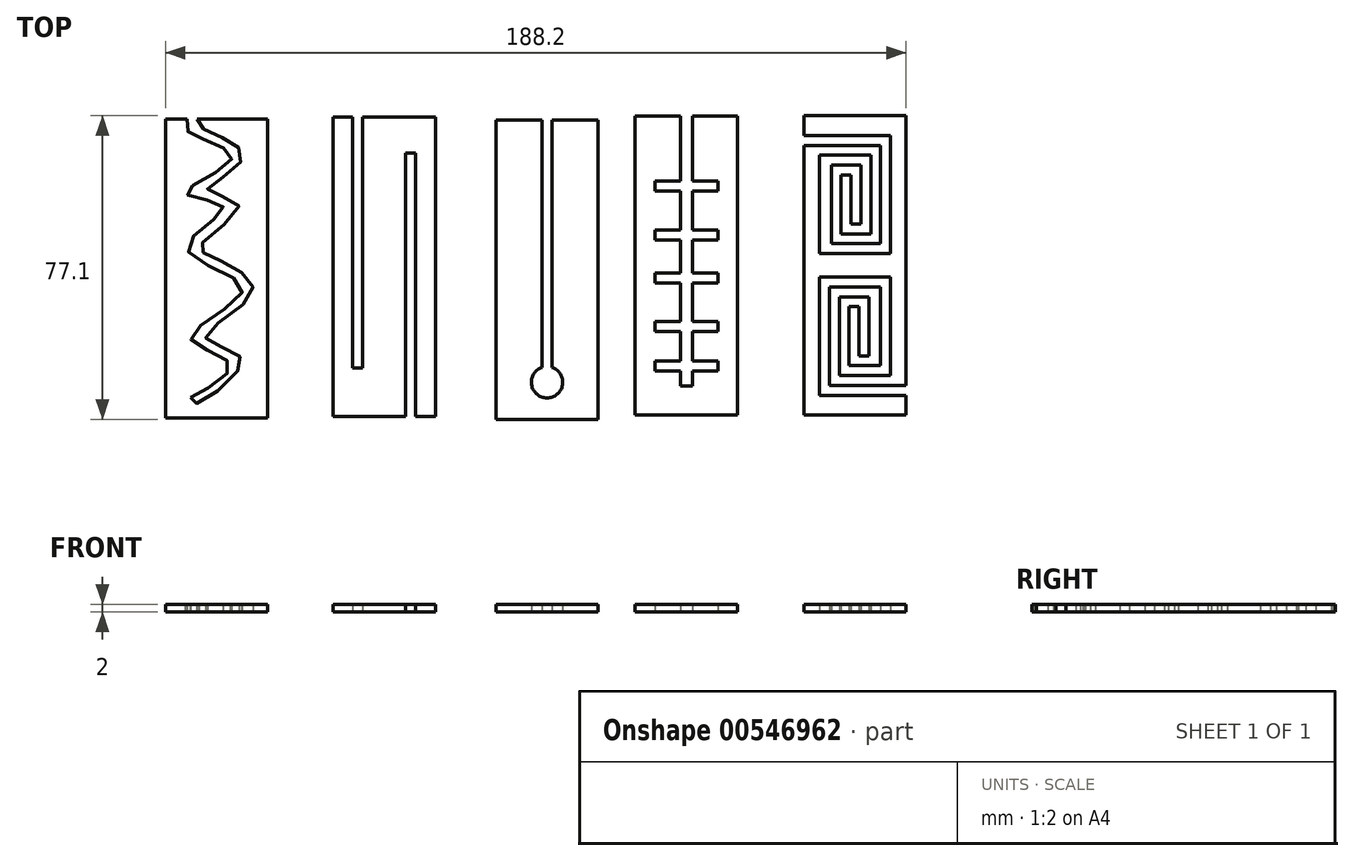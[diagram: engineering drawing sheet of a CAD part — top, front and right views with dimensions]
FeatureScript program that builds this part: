
annotation { "Feature Type Name" : "Feature", "Feature Type Description" : "" }
export const myFeature = defineFeature(function(context is Context, id is Id, definition is map)
    precondition{}
    {
        {
            var Q0;
            Q0=qCreatedBy(makeId("Top.planeOp"),FACE);
            var sketch = newSketch(context, id + "F0", { "sketchPlane" : qUnion([Q0])});
            skLineSegment(sketch, "E0.bottom", {"start": v(-60.07, 57.75) * mm, "end": v(-34.07, 57.75) * mm});
            skLineSegment(sketch, "E0.top", {"start": v(-60.07, -18.25) * mm, "end": v(-34.07, -18.25) * mm});
            skLineSegment(sketch, "E0.left", {"start": v(-60.07, 57.75) * mm, "end": v(-60.07, -18.25) * mm});
            skLineSegment(sketch, "E0.right", {"start": v(-34.07, 57.75) * mm, "end": v(-34.07, -18.25) * mm});
            skFitSpline(sketch, "E1", {"points": [v(-54.5, 57.75) * mm, v(-52.59, 53.49) * mm, v(-43.2, 47.62) * mm, v(-54.81, 38.91) * mm, v(-45.36, 35.29) * mm, v(-54.59, 24.98) * mm, v(-40.4, 14.57) * mm, v(-53.66, 2.1) * mm, v(-43.58, -4.75) * mm, v(-53.63, -13.02) * mm], "startDerivative": vector(-39.3, -111.57) * mm, "endDerivative": vector(-54.15, -27.59) * mm});
            skFitSpline(sketch, "E2", {"points": [v(-52, 57.75) * mm, v(-49.93, 55) * mm, v(-41.52, 50.54) * mm, v(-41.87, 45.6) * mm, v(-49.3, 39.6) * mm, v(-41.4, 35.83) * mm, v(-51.17, 25.7) * mm, v(-50.23, 23.7) * mm, v(-40.34, 18.4) * mm, v(-38.46, 12.52) * mm, v(-49.88, 2.4) * mm, v(-42, -1.84) * mm, v(-41.64, -6.2) * mm, v(-52.86, -14.54) * mm, v(-53.63, -13.02) * mm], "startDerivative": vector(-29.1, -66.37) * mm, "endDerivative": vector(-0.83, 52.83) * mm});
            skLineSegment(sketch, "E3.bottom", {"start": v(-17.5, 58.21) * mm, "end": v(8.5, 58.21) * mm});
            skLineSegment(sketch, "E3.top", {"start": v(-17.5, -17.79) * mm, "end": v(8.5, -17.79) * mm});
            skLineSegment(sketch, "E3.left", {"start": v(-17.5, 58.21) * mm, "end": v(-17.5, -17.79) * mm});
            skLineSegment(sketch, "E3.right", {"start": v(8.5, 58.21) * mm, "end": v(8.5, -17.79) * mm});
            skLineSegment(sketch, "E4.bottom", {"start": v(23.9, 57.45) * mm, "end": v(35.64, 57.45) * mm});
            skLineSegment(sketch, "E4.top", {"start": v(23.9, -18.55) * mm, "end": v(49.9, -18.55) * mm});
            skLineSegment(sketch, "E4.left", {"start": v(23.9, 57.45) * mm, "end": v(23.9, -18.55) * mm});
            skLineSegment(sketch, "E4.right", {"start": v(49.9, 57.45) * mm, "end": v(49.9, -18.55) * mm});
            skLineSegment(sketch, "E5.bottom", {"start": v(59.3, 58.49) * mm, "end": v(70.8, 58.49) * mm});
            skLineSegment(sketch, "E5.top", {"start": v(59.3, -17.51) * mm, "end": v(85.3, -17.51) * mm});
            skLineSegment(sketch, "E5.left", {"start": v(59.3, 58.49) * mm, "end": v(59.3, -17.51) * mm});
            skLineSegment(sketch, "E5.right", {"start": v(85.3, 58.49) * mm, "end": v(85.3, -17.51) * mm});
            skLineSegment(sketch, "E6.bottom", {"start": v(102.13, 58.55) * mm, "end": v(128.13, 58.55) * mm});
            skLineSegment(sketch, "E6.top", {"start": v(102.13, -17.45) * mm, "end": v(128.13, -17.45) * mm});
            skLineSegment(sketch, "E6.left", {"start": v(102.13, 58.55) * mm, "end": v(102.13, -17.45) * mm});
            skLineSegment(sketch, "E6.right", {"start": v(128.13, 58.55) * mm, "end": v(128.13, -17.45) * mm});
            skLineSegment(sketch, "E7", {"start": v(-12.5, 58.21) * mm, "end": v(-12.5, -5.58) * mm});
            skLineSegment(sketch, "E8", {"start": v(-12.5, -5.58) * mm, "end": v(-10, -5.58) * mm});
            skLineSegment(sketch, "E9", {"start": v(-10, -5.58) * mm, "end": v(-10, 58.21) * mm});
            skLineSegment(sketch, "E10", {"start": v(1, -17.79) * mm, "end": v(1, 49.05) * mm});
            skLineSegment(sketch, "E11", {"start": v(1, 49.05) * mm, "end": v(3.5, 49.05) * mm});
            skLineSegment(sketch, "E12", {"start": v(3.5, 49.05) * mm, "end": v(3.5, -17.79) * mm});
            skLineSegment(sketch, "E13", {"start": v(35.64, 57.45) * mm, "end": v(35.64, -5.35) * mm});
            skLineSegment(sketch, "E14", {"start": v(38.14, 57.45) * mm, "end": v(38.14, -5.36) * mm});
            skLineSegment(sketch, "E15.trimOffspring", {"start": v(38.14, 57.45) * mm, "end": v(49.9, 57.45) * mm});
            skCircle(sketch, "E16", {"center": v(36.89, -9.15) * mm, "radius": 4 * mm});
            skLineSegment(sketch, "E17", {"start": v(70.8, 58.49) * mm, "end": v(70.8, -10.15) * mm});
            skLineSegment(sketch, "E18", {"start": v(70.8, -10.15) * mm, "end": v(73.8, -10.15) * mm});
            skLineSegment(sketch, "E19", {"start": v(73.8, -10.15) * mm, "end": v(73.8, 58.49) * mm});
            skLineSegment(sketch, "E20.trimOffspring", {"start": v(73.8, 58.49) * mm, "end": v(85.3, 58.49) * mm});
            skLineSegment(sketch, "E21", {"start": v(64.3, 41.96) * mm, "end": v(80.3, 41.96) * mm});
            skLineSegment(sketch, "E22", {"start": v(80.3, 41.96) * mm, "end": v(80.3, 39.46) * mm});
            skLineSegment(sketch, "E23", {"start": v(80.3, 39.46) * mm, "end": v(64.3, 39.46) * mm});
            skLineSegment(sketch, "E24", {"start": v(64.3, 39.46) * mm, "end": v(64.3, 41.96) * mm});
            skLineSegment(sketch, "E25", {"start": v(64.3, 29.49) * mm, "end": v(80.3, 29.49) * mm});
            skLineSegment(sketch, "E26", {"start": v(80.3, 29.49) * mm, "end": v(80.3, 26.99) * mm});
            skLineSegment(sketch, "E27", {"start": v(80.3, 26.99) * mm, "end": v(64.3, 26.99) * mm});
            skLineSegment(sketch, "E28", {"start": v(64.3, 26.99) * mm, "end": v(64.3, 29.49) * mm});
            skLineSegment(sketch, "E29", {"start": v(64.3, 58.49) * mm, "end": v(64.3, -17.51) * mm, "construction": true});
            skLineSegment(sketch, "E30", {"start": v(80.3, 58.49) * mm, "end": v(80.3, -17.51) * mm, "construction": true});
            skLineSegment(sketch, "E31", {"start": v(64.3, 18.62) * mm, "end": v(80.3, 18.62) * mm});
            skLineSegment(sketch, "E32", {"start": v(80.3, 18.62) * mm, "end": v(80.3, 16.12) * mm});
            skLineSegment(sketch, "E33", {"start": v(80.3, 16.12) * mm, "end": v(64.3, 16.12) * mm});
            skLineSegment(sketch, "E34", {"start": v(64.3, 16.12) * mm, "end": v(64.3, 18.62) * mm});
            skLineSegment(sketch, "E35", {"start": v(64.3, -3.75) * mm, "end": v(80.3, -3.75) * mm});
            skLineSegment(sketch, "E36", {"start": v(80.3, -3.75) * mm, "end": v(80.3, -6.25) * mm});
            skLineSegment(sketch, "E37", {"start": v(80.3, -6.25) * mm, "end": v(64.3, -6.25) * mm});
            skLineSegment(sketch, "E38", {"start": v(64.3, -6.25) * mm, "end": v(64.3, -3.75) * mm});
            skLineSegment(sketch, "E39", {"start": v(64.3, 6.23) * mm, "end": v(80.3, 6.23) * mm});
            skLineSegment(sketch, "E40", {"start": v(80.3, 6.23) * mm, "end": v(80.3, 3.73) * mm});
            skLineSegment(sketch, "E41", {"start": v(80.3, 3.73) * mm, "end": v(64.3, 3.73) * mm});
            skLineSegment(sketch, "E42", {"start": v(64.3, 3.73) * mm, "end": v(64.3, 6.23) * mm});
            skLineSegment(sketch, "E43", {"start": v(91.15, 26.09) * mm, "end": v(91.15, 23.59) * mm});
            skLineSegment(sketch, "E44.bottom", {"start": v(102.13, 53.55) * mm, "end": v(128.13, 53.55) * mm, "construction": true});
            skLineSegment(sketch, "E44.top", {"start": v(102.13, 23.55) * mm, "end": v(128.13, 23.55) * mm, "construction": true});
            skLineSegment(sketch, "E44.left", {"start": v(102.13, 53.55) * mm, "end": v(102.13, 23.55) * mm, "construction": true});
            skLineSegment(sketch, "E44.right", {"start": v(128.13, 53.55) * mm, "end": v(128.13, 23.55) * mm, "construction": true});
            skLineSegment(sketch, "E45.bottom", {"start": v(102.13, -12.45) * mm, "end": v(128.13, -12.45) * mm, "construction": true});
            skLineSegment(sketch, "E45.top", {"start": v(102.13, 17.55) * mm, "end": v(128.13, 17.55) * mm, "construction": true});
            skLineSegment(sketch, "E45.left", {"start": v(102.13, -12.45) * mm, "end": v(102.13, 17.55) * mm, "construction": true});
            skLineSegment(sketch, "E45.right", {"start": v(128.13, -12.45) * mm, "end": v(128.13, 17.55) * mm, "construction": true});
            skLineSegment(sketch, "E46", {"start": v(124.13, 58.55) * mm, "end": v(124.13, -17.45) * mm, "construction": true});
            skLineSegment(sketch, "E47", {"start": v(106.13, 58.55) * mm, "end": v(106.13, -17.45) * mm, "construction": true});
            skLineSegment(sketch, "E48", {"start": v(102.13, 53.55) * mm, "end": v(124.13, 53.55) * mm});
            skLineSegment(sketch, "E49", {"start": v(124.13, 53.55) * mm, "end": v(124.13, 23.55) * mm});
            skLineSegment(sketch, "E50", {"start": v(124.13, 23.55) * mm, "end": v(106.13, 23.55) * mm});
            skLineSegment(sketch, "E51", {"start": v(106.13, 23.55) * mm, "end": v(106.13, 48.55) * mm});
            skLineSegment(sketch, "E52", {"start": v(106.13, 48.55) * mm, "end": v(119.13, 48.55) * mm});
            skLineSegment(sketch, "E53", {"start": v(102.13, 51.05) * mm, "end": v(121.63, 51.05) * mm});
            skLineSegment(sketch, "E54", {"start": v(121.63, 51.05) * mm, "end": v(121.63, 26.05) * mm});
            skLineSegment(sketch, "E55", {"start": v(121.63, 26.05) * mm, "end": v(109.13, 26.05) * mm});
            skLineSegment(sketch, "E56", {"start": v(109.13, 26.05) * mm, "end": v(109.13, 46.05) * mm});
            skLineSegment(sketch, "E57", {"start": v(109.13, 46.05) * mm, "end": v(116.63, 46.05) * mm});
            skLineSegment(sketch, "E58", {"start": v(119.13, 48.55) * mm, "end": v(119.13, 28.55) * mm});
            skLineSegment(sketch, "E59", {"start": v(119.13, 28.55) * mm, "end": v(111.63, 28.55) * mm});
            skLineSegment(sketch, "E60", {"start": v(111.63, 28.55) * mm, "end": v(111.63, 43.55) * mm});
            skLineSegment(sketch, "E61", {"start": v(116.63, 46.05) * mm, "end": v(116.63, 31.05) * mm});
            skLineSegment(sketch, "E62", {"start": v(116.63, 31.05) * mm, "end": v(114.13, 31.05) * mm});
            skLineSegment(sketch, "E63", {"start": v(114.13, 31.05) * mm, "end": v(114.13, 43.55) * mm});
            skLineSegment(sketch, "E64", {"start": v(111.63, 43.55) * mm, "end": v(114.13, 43.55) * mm});
            skLineSegment(sketch, "E65", {"start": v(128.13, -12.45) * mm, "end": v(106.13, -12.45) * mm});
            skLineSegment(sketch, "E66", {"start": v(106.13, -12.45) * mm, "end": v(106.13, 17.55) * mm});
            skLineSegment(sketch, "E67", {"start": v(106.13, 17.55) * mm, "end": v(124.13, 17.55) * mm});
            skLineSegment(sketch, "E68", {"start": v(124.13, 17.55) * mm, "end": v(124.13, -7.45) * mm});
            skLineSegment(sketch, "E69", {"start": v(124.13, -7.45) * mm, "end": v(111.13, -7.45) * mm});
            skLineSegment(sketch, "E70", {"start": v(111.13, -7.45) * mm, "end": v(111.13, 12.55) * mm});
            skLineSegment(sketch, "E71", {"start": v(111.13, 12.55) * mm, "end": v(118.63, 12.55) * mm});
            skLineSegment(sketch, "E72", {"start": v(118.63, 12.55) * mm, "end": v(118.63, -2.45) * mm});
            skLineSegment(sketch, "E73", {"start": v(118.63, -2.45) * mm, "end": v(116.13, -2.45) * mm});
            skLineSegment(sketch, "E74", {"start": v(128.13, -9.95) * mm, "end": v(108.63, -9.95) * mm});
            skLineSegment(sketch, "E75", {"start": v(108.63, -9.95) * mm, "end": v(108.63, 15.05) * mm});
            skLineSegment(sketch, "E76", {"start": v(108.63, 15.05) * mm, "end": v(121.63, 15.05) * mm});
            skLineSegment(sketch, "E77", {"start": v(121.63, 15.05) * mm, "end": v(121.63, -4.95) * mm});
            skLineSegment(sketch, "E78", {"start": v(121.63, -4.95) * mm, "end": v(113.63, -4.95) * mm});
            skLineSegment(sketch, "E79", {"start": v(113.63, -4.95) * mm, "end": v(113.63, 10.05) * mm});
            skLineSegment(sketch, "E80", {"start": v(113.63, 10.05) * mm, "end": v(116.13, 10.05) * mm});
            skLineSegment(sketch, "E81", {"start": v(116.13, 10.05) * mm, "end": v(116.13, -2.45) * mm});
            skSolve(sketch);
        }
        {
            var Q0;
            Q0=makeQuery(id+"F0.imprint","IMPRINT",FACE,{"disambiguationData":[TD([[makeQuery(id+"F0.imprint","IMPRINT",EDGE,{"derivedFrom":sQuery(id+"F0.wireOp",EDGE,"E0.top")}),1.0]])]});
            var Q1;
            {var subQ1=sQuery(id+"F0.wireOp",EDGE,"E3.left");Q1=makeQuery(id+"F0.imprint","IMPRINT",FACE,{"disambiguationData":[TD([[makeQuery(id+"F0.imprint","IMPRINT",EDGE,{"derivedFrom":subQ1}),1.0]])]});}
            var Q2;
            Q2=makeQuery(id+"F0.imprint","IMPRINT",FACE,{"disambiguationData":[TD([[makeQuery(id+"F0.imprint","IMPRINT",EDGE,{"derivedFrom":sQuery(id+"F0.wireOp",EDGE,"E4.bottom")}),-1.0]])]});
            var Q3;
            {var subQ37=sQuery(id+"F0.wireOp",EDGE,"E5.bottom");Q3=makeQuery(id+"F0.imprint","IMPRINT",FACE,{"disambiguationData":[TD([[makeQuery(id+"F0.imprint","IMPRINT",EDGE,{"derivedFrom":subQ37}),-1.0]])]});}
            var Q4;
            {var subQ4=sQuery(id+"F0.wireOp",EDGE,"E6.bottom");Q4=makeQuery(id+"F0.imprint","IMPRINT",FACE,{"disambiguationData":[TD([[makeQuery(id+"F0.imprint","IMPRINT",EDGE,{"derivedFrom":subQ4}),-1.0]])]});}
            extrude(context, id + "F1", {"entities" : qUnion([Q0, Q1, Q2, Q3, Q4]), "depth" : 2 * mm, "offsetDistance" : 25 * mm});
        }
    });
